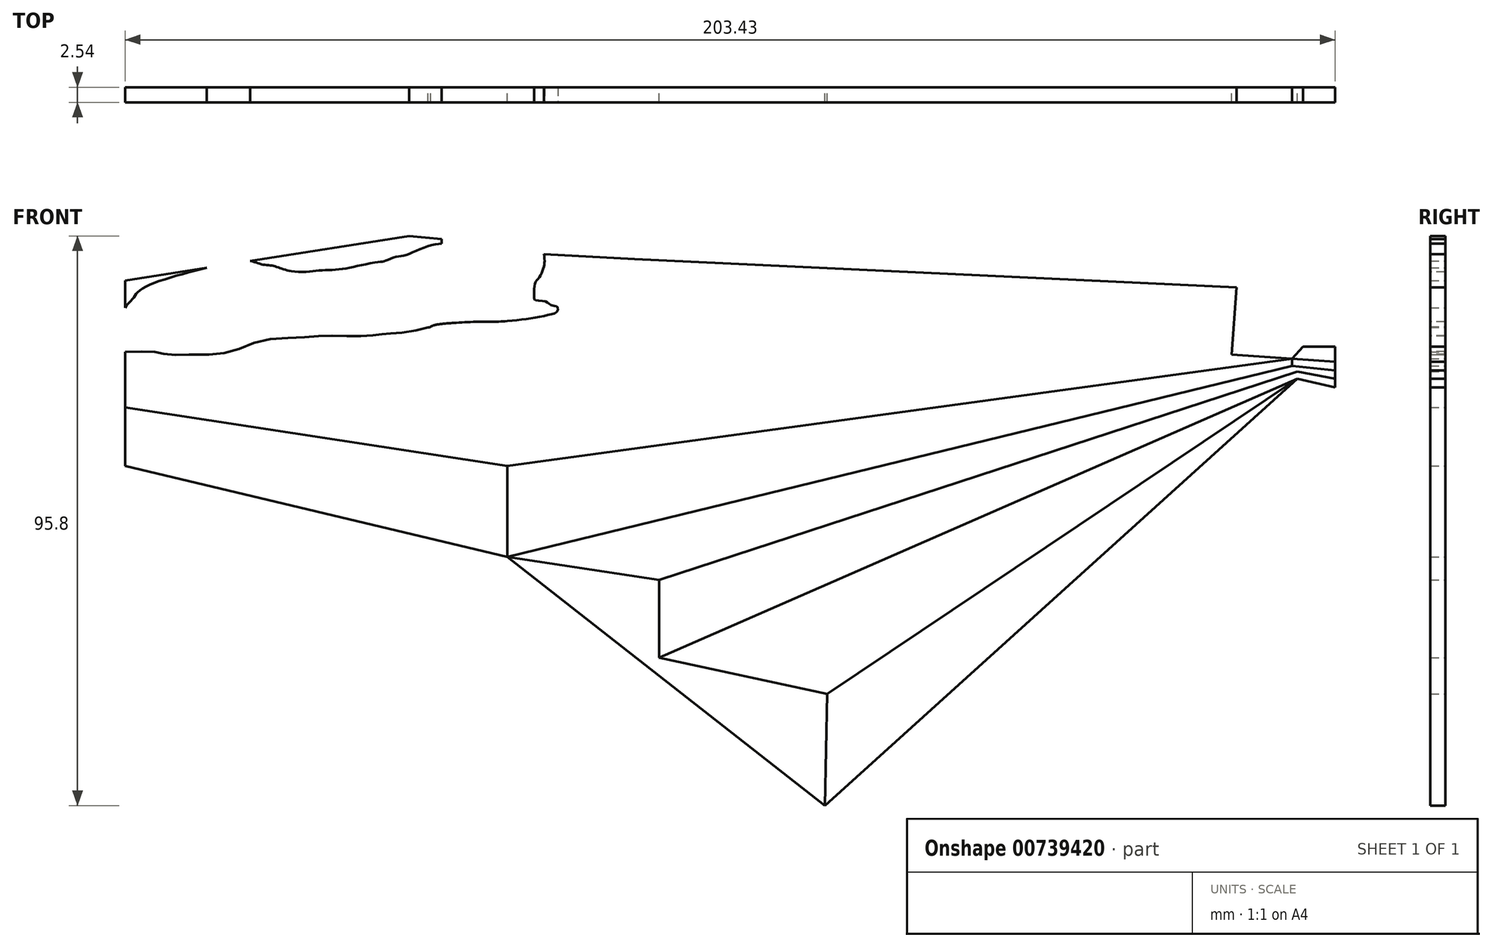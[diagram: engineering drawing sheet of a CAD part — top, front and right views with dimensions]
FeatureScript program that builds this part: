
annotation { "Feature Type Name" : "Feature", "Feature Type Description" : "" }
export const myFeature = defineFeature(function(context is Context, id is Id, definition is map)
    precondition{}
    {
        {
            var Q0;
            Q0=qCreatedBy(makeId("Front.planeOp"),FACE);
            var sketch = newSketch(context, id + "F0", { "sketchPlane" : qUnion([Q0])});
            skSolve(sketch);
        }
        {
            var Q0;
            Q0=qCreatedBy(makeId("Front.planeOp"),FACE);
            var sketch = newSketch(context, id + "F1", { "sketchPlane" : qUnion([Q0])});
            skPoint(sketch, "E0.0", {"position": v(-103.73, 76.7) * mm});
            skPoint(sketch, "E1.0", {"position": v(99.7, 76.7) * mm});
            skPoint(sketch, "E2.0", {"position": v(99.7, -75.88) * mm});
            skPoint(sketch, "E3.0", {"position": v(-103.73, -75.88) * mm});
            skLineSegment(sketch, "E4", {"start": v(-103.73, 76.7) * mm, "end": v(99.7, 76.7) * mm});
            skLineSegment(sketch, "E5", {"start": v(99.7, 76.7) * mm, "end": v(99.7, -75.88) * mm});
            skLineSegment(sketch, "E6", {"start": v(99.7, -75.88) * mm, "end": v(-103.73, -75.88) * mm});
            skLineSegment(sketch, "E7", {"start": v(-103.73, 76.7) * mm, "end": v(-103.73, -75.88) * mm});
            skLineSegment(sketch, "E8", {"start": v(-39.5, -34.03) * mm, "end": v(-39.5, -18.76) * mm});
            skLineSegment(sketch, "E9", {"start": v(-39.5, -18.76) * mm, "end": v(-103.73, -8.88) * mm});
            skLineSegment(sketch, "E10", {"start": v(-39.5, -34.03) * mm, "end": v(-103.73, -18.76) * mm});
            skLineSegment(sketch, "E11", {"start": v(87.73, 76.7) * mm, "end": v(82.34, 0) * mm});
            skLineSegment(sketch, "E12", {"start": v(82.34, 0) * mm, "end": v(92.46, -0.71) * mm});
            skLineSegment(sketch, "E13", {"start": v(92.46, -0.71) * mm, "end": v(99.7, 76.7) * mm});
            skLineSegment(sketch, "E14", {"start": v(92.46, -0.71) * mm, "end": v(94.3, 1.29) * mm});
            skLineSegment(sketch, "E15", {"start": v(94.3, 1.29) * mm, "end": v(99.7, 63.93) * mm});
            skLineSegment(sketch, "E16", {"start": v(-39.5, -34.03) * mm, "end": v(-13.95, -37.95) * mm});
            skLineSegment(sketch, "E17", {"start": v(-13.95, -51.01) * mm, "end": v(-13.95, -37.95) * mm});
            skLineSegment(sketch, "E18", {"start": v(23.89, -66.32) * mm, "end": v(13.9, -75.88) * mm});
            skLineSegment(sketch, "E19", {"start": v(14.27, -57.12) * mm, "end": v(13.9, -75.88) * mm});
            skLineSegment(sketch, "E20", {"start": v(13.9, -75.88) * mm, "end": v(-39.5, -34.03) * mm});
            skLineSegment(sketch, "E21", {"start": v(-53.97, 76.7) * mm, "end": v(-50.52, 18.62) * mm});
            skLineSegment(sketch, "E22", {"start": v(-18.08, 54.06) * mm, "end": v(-18.08, 16.56) * mm});
            skLineSegment(sketch, "E23", {"start": v(-18.08, 54.06) * mm, "end": v(87.24, 69.82) * mm});
            skLineSegment(sketch, "E24", {"start": v(87.16, 68.7) * mm, "end": v(-15.41, 52.8) * mm});
            skLineSegment(sketch, "E25", {"start": v(-15.41, 52.8) * mm, "end": v(-18.08, 54.06) * mm});
            skLineSegment(sketch, "E26", {"start": v(-18.08, 16.56) * mm, "end": v(83.17, 11.8) * mm});
            skLineSegment(sketch, "E27", {"start": v(-18.08, 16.02) * mm, "end": v(83.13, 11.27) * mm});
            skLineSegment(sketch, "E28", {"start": v(-18.08, 16.56) * mm, "end": v(-35.62, 17.39) * mm});
            skLineSegment(sketch, "E29", {"start": v(-55.98, 19.92) * mm, "end": v(-50.56, 19.4) * mm});
            skLineSegment(sketch, "E30", {"start": v(-55.98, 19.92) * mm, "end": v(-103.73, 12.41) * mm});
            skPoint(sketch, "E31.1.internal.snap0", {"position": v(-103.73, 0.4) * mm});
            skPoint(sketch, "E31.5.internal.snap0", {"position": v(-103.73, 0.4) * mm});
            skFitSpline(sketch, "E31", {"points": [v(-103.73, 0.4) * mm, v(-98.66, 0.4) * mm, v(-96.75, 0) * mm, v(-92.82, 0) * mm, v(-91.02, 0) * mm, v(-86.24, 0.4) * mm, v(-80.72, 2.33) * mm, v(-73.82, 2.86) * mm, v(-69.36, 3.18) * mm, v(-64.47, 3.07) * mm, v(-61.4, 3.28) * mm, v(-59.7, 3.5) * mm, v(-56.93, 3.7) * mm, v(-52.8, 4.56) * mm, v(-51.52, 4.98) * mm, v(-48.55, 5.3) * mm, v(-43.77, 5.51) * mm, v(-41.33, 5.51) * mm, v(-38.25, 5.72) * mm, v(-35.06, 6.15) * mm, v(-32.4, 6.68) * mm, v(-31.13, 7.21) * mm, v(-31.03, 7.95) * mm, v(-31.56, 8.17) * mm, v(-32.62, 8.6) * mm, v(-33.04, 8.9) * mm, v(-34.74, 9.12) * mm, v(-34.96, 9.44) * mm, v(-34.96, 10.6) * mm, v(-34.74, 12.2) * mm, v(-34.1, 12.94) * mm, v(-33.47, 14.32) * mm, v(-33.26, 15.28) * mm, v(-33.26, 16.45) * mm, v(-33.56, 17.29) * mm, v(-34.22, 17.32) * mm, v(-35.62, 17.39) * mm, v(-37.93, 19) * mm, v(-40, 19.45) * mm, v(-42.39, 19.63) * mm, v(-44.62, 19.63) * mm, v(-45.9, 19.63) * mm, v(-48.97, 18.46) * mm, v(-50.52, 18.62) * mm, v(-53.85, 17.83) * mm, v(-56.83, 16.66) * mm, v(-58.42, 16.34) * mm, v(-60.12, 15.7) * mm, v(-60.76, 15.6) * mm, v(-63.84, 15.07) * mm, v(-66.8, 14.43) * mm, v(-69.14, 14.22) * mm, v(-71.16, 14.11) * mm, v(-73.18, 13.9) * mm, v(-75.83, 14) * mm, v(-77.74, 14.54) * mm, v(-79.12, 14.96) * mm, v(-80.82, 15.17) * mm, v(-82.72, 15.72) * mm, v(-90.04, 14.57) * mm, v(-101.1, 10.93) * mm, v(-102.48, 9.33) * mm, v(-103.73, 7.85) * mm, v(-103.73, 5.94) * mm], "startDerivative": vector(249.33, 11.05) * mm, "endDerivative": vector(25, -140.73) * mm});
            skFitSpline(sketch, "E32", {"points": [v(-75.83, 14) * mm, v(-72.22, 12.94) * mm, v(-70.2, 12.94) * mm, v(-68.08, 12.84) * mm, v(-66.38, 12.2) * mm, v(-63.84, 12.41) * mm, v(-60.54, 12.63) * mm, v(-58, 12.2) * mm, v(-57.46, 12.1) * mm, v(-56.08, 11.14) * mm, v(-55.02, 8.6) * mm, v(-53.64, 6.9) * mm, v(-52.35, 4.7) * mm, v(-52.8, 4.56) * mm], "startDerivative": vector(37.33, -13.2) * mm, "endDerivative": vector(-15.78, -1.82) * mm});
            skFitSpline(sketch, "E33", {"points": [v(-38.34, 8.38) * mm, v(-35.64, 8.08) * mm, v(-34.74, 9.12) * mm], "startDerivative": vector(5.34, -1.4) * mm, "endDerivative": vector(1.64, 3.13) * mm});
            skFitSpline(sketch, "E34", {"points": [v(-39.45, 5.61) * mm, v(-38.34, 8.38) * mm, v(-38.34, 11.01) * mm, v(-39.1, 13.19) * mm, v(-40, 14.09) * mm, v(-41.87, 15.44) * mm, v(-43.45, 15.9) * mm, v(-44.95, 15.9) * mm, v(-46.75, 15.82) * mm, v(-48.55, 15.3) * mm, v(-50.43, 13.41) * mm, v(-50.88, 11.54) * mm, v(-51.03, 9.81) * mm, v(-49.3, 6.15) * mm, v(-48.55, 5.3) * mm], "startDerivative": vector(16.72, 29.99) * mm, "endDerivative": vector(12.47, -11.38) * mm});
            skFitSpline(sketch, "E35", {"points": [v(-55.02, 8.6) * mm, v(-53.96, 9.81) * mm, v(-52.6, 10.26) * mm, v(-51.03, 9.81) * mm], "startDerivative": vector(2.86, 4) * mm, "endDerivative": vector(4.64, -1.92) * mm});
            skFitSpline(sketch, "E36", {"points": [v(-66.38, 12.2) * mm, v(-64.41, 13.1) * mm, v(-63.75, 13.5) * mm, v(-63.27, 14.32) * mm, v(-63, 14.74) * mm, v(-61.79, 15.45) * mm], "startDerivative": vector(7.92, 3.65) * mm, "endDerivative": vector(6.51, 3.2) * mm});
            skLineSegment(sketch, "E37", {"start": v(-42.83, 65.92) * mm, "end": v(0, 76.7) * mm});
            skLineSegment(sketch, "E38", {"start": v(-41.93, 65.3) * mm, "end": v(4.14, 76.7) * mm});
            skLineSegment(sketch, "E39", {"start": v(-46.08, 76.7) * mm, "end": v(-44.62, 19.63) * mm});
            skLineSegment(sketch, "E40", {"start": v(-42.83, 65.92) * mm, "end": v(-42.39, 19.63) * mm});
            skLineSegment(sketch, "E41", {"start": v(-41.93, 65.3) * mm, "end": v(-42.82, 65.08) * mm});
            skLineSegment(sketch, "E42", {"start": v(-42.82, 65.08) * mm, "end": v(-41.16, 64.56) * mm});
            skLineSegment(sketch, "E43", {"start": v(-40, 19.45) * mm, "end": v(-41.16, 64.56) * mm});
            skLineSegment(sketch, "E44", {"start": v(2.24, 43.2) * mm, "end": v(2.4, 26.62) * mm});
            skLineSegment(sketch, "E45", {"start": v(2.4, 26.62) * mm, "end": v(13.27, 25.94) * mm});
            skLineSegment(sketch, "E46", {"start": v(13.27, 25.94) * mm, "end": v(13.12, 41.85) * mm});
            skLineSegment(sketch, "E47", {"start": v(13.12, 41.85) * mm, "end": v(2.24, 43.2) * mm});
            skLineSegment(sketch, "E48", {"start": v(10.75, 26.1) * mm, "end": v(10.97, 41.5) * mm});
            skLineSegment(sketch, "E49", {"start": v(10.97, 41.5) * mm, "end": v(13.12, 41.85) * mm});
            skLineSegment(sketch, "E50", {"start": v(10.97, 41.5) * mm, "end": v(2.24, 42.7) * mm});
            skLineSegment(sketch, "E51", {"start": v(-15.41, 52.8) * mm, "end": v(-15.41, 16.44) * mm});
            skLineSegment(sketch, "E52", {"start": v(-18.08, 16.02) * mm, "end": v(-33.33, 16.85) * mm});
            skLineSegment(sketch, "E53", {"start": v(-39.5, -18.76) * mm, "end": v(92.46, -0.71) * mm});
            skLineSegment(sketch, "E54", {"start": v(-39.5, -34.03) * mm, "end": v(92.46, -1.9) * mm});
            skLineSegment(sketch, "E55", {"start": v(-13.95, -51.01) * mm, "end": v(93.34, -4.07) * mm});
            skLineSegment(sketch, "E56", {"start": v(93.34, -2.85) * mm, "end": v(93.34, -4.07) * mm});
            skLineSegment(sketch, "E57", {"start": v(92.46, -0.71) * mm, "end": v(92.46, -1.9) * mm});
            skLineSegment(sketch, "E58", {"start": v(92.46, -1.9) * mm, "end": v(93.34, -2.85) * mm});
            skLineSegment(sketch, "E59", {"start": v(93.34, -2.85) * mm, "end": v(-13.95, -37.95) * mm});
            skLineSegment(sketch, "E60", {"start": v(13.9, -75.88) * mm, "end": v(93.34, -4.07) * mm});
            skLineSegment(sketch, "E61", {"start": v(14.27, -57.12) * mm, "end": v(93.34, -4.07) * mm});
            skLineSegment(sketch, "E62", {"start": v(-13.95, -51.01) * mm, "end": v(14.27, -57.12) * mm});
            skLineSegment(sketch, "E63", {"start": v(93.34, -4.07) * mm, "end": v(99.7, -5.56) * mm});
            skLineSegment(sketch, "E64", {"start": v(93.34, -2.85) * mm, "end": v(99.7, -4.07) * mm});
            skLineSegment(sketch, "E65", {"start": v(92.46, -0.71) * mm, "end": v(99.7, -1.22) * mm});
            skPoint(sketch, "E66.endSnap0", {"position": v(92.9, -2.38) * mm});
            skLineSegment(sketch, "E67", {"start": v(92.46, -1.9) * mm, "end": v(99.7, -2.7) * mm});
            skLineSegment(sketch, "E68", {"start": v(94.3, 1.29) * mm, "end": v(99.7, 1.29) * mm});
            skLineSegment(sketch, "E69", {"start": v(-39.5, -18.76) * mm, "end": v(-39.5, -34.03) * mm});
            skSolve(sketch);
        }
        {
            var Q0;
            {var subQ11=sQuery(id+"F1.wireOp",EDGE,"E9");Q0=makeQuery(id+"F1.imprint","IMPRINT",FACE,{"disambiguationData":[TD([[makeQuery(id+"F1.imprint","IMPRINT",EDGE,{"derivedFrom":subQ11}),-1.0]])]});}
            var Q1;
            {var subQ5=sQuery(id+"F1.wireOp",EDGE,"E29");Q1=makeQuery(id+"F1.imprint","IMPRINT",FACE,{"disambiguationData":[TD([[makeQuery(id+"F1.imprint","IMPRINT",EDGE,{"derivedFrom":subQ5}),-1.0]])]});}
            var Q2;
            {var subQ0=sQuery(id+"F1.wireOp",EDGE,"E30");var subQ1=sQuery(id+"F1.wireOp",EDGE,"E7");var subQ2=makeQuery(id+"F1.imprint","INTERSECT",VERTEX,{"derivedFrom":[subQ1,subQ0]});Q2=makeQuery(id+"F1.imprint","IMPRINT",FACE,{"disambiguationData":[TD([[makeQuery(id+"F1.imprint","IMPRINT",EDGE,{"disambiguationData":[TD([[subQ2,-1.0]])],"derivedFrom":subQ1}),1.0]])]});}
            var Q3;
            Q3=makeQuery(id+"F1.imprint","IMPRINT",FACE,{"disambiguationData":[TD([[makeQuery(id+"F1.imprint","IMPRINT",EDGE,{"derivedFrom":sQuery(id+"F1.wireOp",EDGE,"E16")}),1.0]])]});
            var Q4;
            Q4=makeQuery(id+"F1.imprint","IMPRINT",FACE,{"disambiguationData":[TD([[makeQuery(id+"F1.imprint","IMPRINT",EDGE,{"derivedFrom":sQuery(id+"F1.wireOp",EDGE,"E55")}),-1.0]])]});
            var Q5;
            Q5=makeQuery(id+"F1.imprint","IMPRINT",FACE,{"disambiguationData":[TD([[makeQuery(id+"F1.imprint","IMPRINT",EDGE,{"derivedFrom":sQuery(id+"F1.wireOp",EDGE,"E58")}),1.0]])]});
            var Q6;
            Q6=makeQuery(id+"F1.imprint","IMPRINT",FACE,{"disambiguationData":[TD([[makeQuery(id+"F1.imprint","IMPRINT",EDGE,{"derivedFrom":sQuery(id+"F1.wireOp",EDGE,"E14")}),-1.0]])]});
            extrude(context, id + "F2", {"entities" : qUnion([Q0, Q1, Q2, Q3, Q4, Q5, Q6]), "depth" : 2.54 * mm, "offsetDistance" : 25.4 * mm});
        }
        {
            var Q0;
            Q0=makeQuery(id+"F1.imprint","IMPRINT",FACE,{"disambiguationData":[TD([[makeQuery(id+"F1.imprint","IMPRINT",EDGE,{"derivedFrom":sQuery(id+"F1.wireOp",EDGE,"E8")}),1.0]])]});
            var Q1;
            Q1=makeQuery(id+"F1.imprint","IMPRINT",FACE,{"disambiguationData":[TD([[makeQuery(id+"F1.imprint","IMPRINT",EDGE,{"derivedFrom":sQuery(id+"F1.wireOp",EDGE,"E8")}),-1.0]])]});
            var Q2;
            Q2=makeQuery(id+"F1.imprint","IMPRINT",FACE,{"disambiguationData":[TD([[makeQuery(id+"F1.imprint","IMPRINT",EDGE,{"derivedFrom":sQuery(id+"F1.wireOp",EDGE,"E57")}),1.0]])]});
            extrude(context, id + "F3", {"entities" : qUnion([Q0, Q1, Q2]), "depth" : 2.54 * mm, "offsetDistance" : 25.4 * mm});
        }
        {
            var Q0;
            Q0=makeQuery(id+"F1.imprint","IMPRINT",FACE,{"disambiguationData":[TD([[makeQuery(id+"F1.imprint","IMPRINT",EDGE,{"derivedFrom":sQuery(id+"F1.wireOp",EDGE,"E17")}),-1.0]])]});
            var Q1;
            Q1=makeQuery(id+"F1.imprint","IMPRINT",FACE,{"disambiguationData":[TD([[makeQuery(id+"F1.imprint","IMPRINT",EDGE,{"derivedFrom":sQuery(id+"F1.wireOp",EDGE,"E56")}),1.0]])]});
            extrude(context, id + "F4", {"entities" : qUnion([Q0, Q1]), "depth" : 2.54 * mm, "offsetDistance" : 25.4 * mm});
        }
        {
            var Q0;
            Q0=makeQuery(id+"F1.imprint","IMPRINT",FACE,{"disambiguationData":[TD([[makeQuery(id+"F1.imprint","IMPRINT",EDGE,{"derivedFrom":sQuery(id+"F1.wireOp",EDGE,"E19")}),1.0]])]});
            extrude(context, id + "F5", {"entities" : qUnion([Q0]), "depth" : 2.54 * mm, "offsetDistance" : 25.4 * mm});
        }
        {
            var Q0;
            Q0=makeQuery(id+"F1.imprint","IMPRINT",FACE,{"disambiguationData":[TD([[makeQuery(id+"F1.imprint","IMPRINT",EDGE,{"derivedFrom":sQuery(id+"F1.wireOp",EDGE,"E16")}),-1.0]])]});
            extrude(context, id + "F6", {"entities" : qUnion([Q0]), "depth" : 2.54 * mm, "offsetDistance" : 25.4 * mm});
        }
        {
            var Q0;
            Q0=makeQuery(id+"F1.imprint","IMPRINT",FACE,{"disambiguationData":[TD([[makeQuery(id+"F1.imprint","IMPRINT",EDGE,{"derivedFrom":sQuery(id+"F1.wireOp",EDGE,"E53")}),-1.0]])]});
            extrude(context, id + "F7", {"entities" : qUnion([Q0]), "depth" : 2.54 * mm, "offsetDistance" : 25.4 * mm});
        }
        {
            var Q0;
            {var subQ0=sQuery(id+"F1.wireOp",EDGE,"E9");Q0=makeQuery(id+"F1.imprint","IMPRINT",FACE,{"disambiguationData":[TD([[makeQuery(id+"F1.imprint","IMPRINT",EDGE,{"derivedFrom":subQ0}),1.0]])]});}
            extrude(context, id + "F8", {"entities" : qUnion([Q0]), "depth" : 2.54 * mm, "offsetDistance" : 25.4 * mm});
        }
    });
